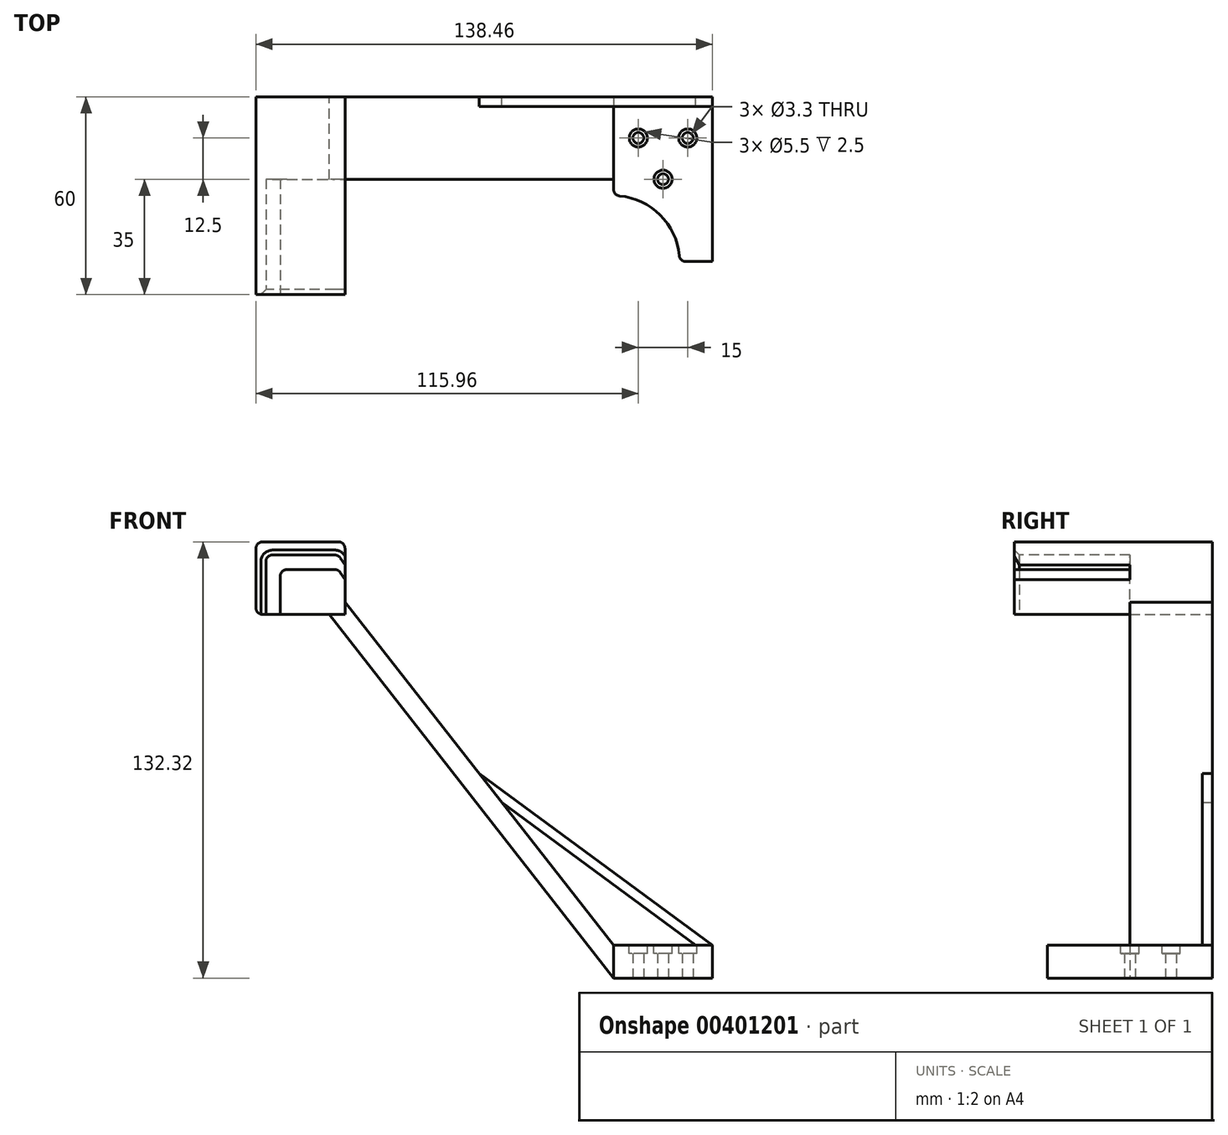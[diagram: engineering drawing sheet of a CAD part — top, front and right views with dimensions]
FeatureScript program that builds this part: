
annotation { "Feature Type Name" : "Feature", "Feature Type Description" : "" }
export const myFeature = defineFeature(function(context is Context, id is Id, definition is map)
    precondition{}
    {
        {
            var Q0;
            Q0=qCreatedBy(makeId("Top.planeOp"),FACE);
            var sketch = newSketch(context, id + "F0", { "sketchPlane" : qUnion([Q0])});
            skLineSegment(sketch, "E0.bottom", {"start": v(0, 0) * mm, "end": v(30, 0) * mm});
            skLineSegment(sketch, "E0.top", {"start": v(0, -50) * mm, "end": v(30, -50) * mm});
            skLineSegment(sketch, "E0.left", {"start": v(0, 0) * mm, "end": v(0, -50) * mm});
            skLineSegment(sketch, "E0.right", {"start": v(30, 0) * mm, "end": v(30, -50) * mm});
            skLineSegment(sketch, "E1", {"start": v(15, -50) * mm, "end": v(15, 0) * mm, "construction": true});
            skLineSegment(sketch, "E2", {"start": v(0, -25) * mm, "end": v(30, -25) * mm, "construction": true});
            skLineSegment(sketch, "E3", {"start": v(0, -12.5) * mm, "end": v(30, -12.5) * mm, "construction": true});
            skPoint(sketch, "E4", {"position": v(7.5, -12.5) * mm});
            skPoint(sketch, "E5", {"position": v(22.5, -12.5) * mm});
            skPoint(sketch, "E6", {"position": v(15, -25) * mm});
            skSolve(sketch);
        }
        {
            var Q0;
            Q0=makeQuery(id+"F0.imprint","IMPRINT",FACE,{"disambiguationData":[TD([[makeQuery(id+"F0.imprint","IMPRINT",EDGE,{"derivedFrom":sQuery(id+"F0.wireOp",EDGE,"E0.bottom")}),-1.0]])]});
            extrude(context, id + "F1", {"entities" : qUnion([Q0]), "depth" : 10 * mm, "offsetDistance" : 25 * mm});
        }
        {
            var Q0;
            Q0=qCreatedBy(makeId("Front.planeOp"),FACE);
            var sketch = newSketch(context, id + "F2", { "sketchPlane" : qUnion([Q0])});
            skLineSegment(sketch, "E7", {"start": v(0, 0) * mm, "end": v(-86.2, 110.32) * mm});
            skLineSegment(sketch, "E8", {"start": v(-86.2, 110.32) * mm, "end": v(-81.46, 114.02) * mm});
            skLineSegment(sketch, "E9", {"start": v(-81.46, 114.02) * mm, "end": v(0, 10) * mm});
            skLineSegment(sketch, "E10", {"start": v(0, 10) * mm, "end": v(0, 0) * mm});
            skLineSegment(sketch, "E11.bottom", {"start": v(-81.46, 132.32) * mm, "end": v(-108.46, 132.32) * mm});
            skLineSegment(sketch, "E11.top", {"start": v(-81.46, 110.32) * mm, "end": v(-108.46, 110.32) * mm});
            skLineSegment(sketch, "E11.left", {"start": v(-81.46, 132.32) * mm, "end": v(-81.46, 110.32) * mm});
            skLineSegment(sketch, "E11.right", {"start": v(-108.46, 132.32) * mm, "end": v(-108.46, 110.32) * mm});
            skSolve(sketch);
        }
        {
            var Q0;
            Q0=makeQuery(id+"F2.imprint","IMPRINT",FACE,{"disambiguationData":[TD([[makeQuery(id+"F2.imprint","IMPRINT",EDGE,{"derivedFrom":sQuery(id+"F2.wireOp",EDGE,"E9")}),-1.0]])]});
            extrude(context, id + "F3", {"entities" : qUnion([Q0]), "operationType" : NewBodyOperationType.ADD, "depth" : 25 * mm, "offsetDistance" : 25 * mm});
        }
        {
            var Q0;
            Q0=makeQuery(id+"F1.opExtrude","CAP_FACE",FACE,{"disambiguationData":[OSD([sQuery(id+"F0.wireOp",EDGE,"E0.bottom"),sQuery(id+"F0.wireOp",EDGE,"E0.top"),sQuery(id+"F0.wireOp",EDGE,"E0.left"),sQuery(id+"F0.wireOp",EDGE,"E0.right")])],"isStart":false});
            var sketch = newSketch(context, id + "F4", { "sketchPlane" : qUnion([Q0])});
            skCircle(sketch, "E12", {"center": v(0, -50) * mm, "radius": 20 * mm});
            skSolve(sketch);
        }
        {
            var Q0;
            Q0 = qSketchRegion(id + "F4", true);
            var Q1;
            {var subQ1=makeQuery(id+"F1.opExtrude","CAP_EDGE",EDGE,{"disambiguationData":[OSD([sQuery(id+"F0.wireOp",EDGE,"E0.left")])],"isStart":false});var subQ2=makeQuery(id+"F3.boolean.opBoolean","SPLIT",EDGE,{"derivedFrom":subQ1});Q1=makeQuery(id+"F4.imprint","IMPRINT",FACE,{"disambiguationData":[TD([[makeQuery(id+"F4.imprint","IMPRINT",EDGE,{"derivedFrom":subQ2}),1.0]])]});}
            extrude(context, id + "F5", {"entities" : qUnion([Q0, Q1]), "operationType" : NewBodyOperationType.REMOVE, "oppositeDirection" : true, "depth" : 25 * mm, "offsetDistance" : 25 * mm});
        }
        {
            var Q0;
            {var subQ4=sQuery(id+"F2.wireOp",EDGE,"E8");Q0=makeQuery(id+"F2.imprint","IMPRINT",FACE,{"disambiguationData":[TD([[makeQuery(id+"F2.imprint","IMPRINT",EDGE,{"derivedFrom":subQ4}),1.0]])]});}
            var Q1;
            {var subQ0=sQuery(id+"F2.wireOp",EDGE,"E8");Q1=makeQuery(id+"F2.imprint","IMPRINT",FACE,{"disambiguationData":[TD([[makeQuery(id+"F2.imprint","IMPRINT",EDGE,{"derivedFrom":subQ0}),-1.0]])]});}
            extrude(context, id + "F6", {"entities" : qUnion([Q0, Q1]), "depth" : 60 * mm, "offsetDistance" : 25 * mm});
        }
        {
            var Q0;
            Q0=makeQuery(id+"F6.opExtrude","CAP_FACE",FACE,{"disambiguationData":[OSD([sQuery(id+"F2.wireOp",EDGE,"E11.bottom"),sQuery(id+"F2.wireOp",EDGE,"E11.top"),sQuery(id+"F2.wireOp",EDGE,"E11.left"),sQuery(id+"F2.wireOp",EDGE,"E11.right")])],"isStart":false});
            var sketch = newSketch(context, id + "F7", { "sketchPlane" : qUnion([Q0])});
            skLineSegment(sketch, "E13", {"start": v(-105.46, 110.32) * mm, "end": v(-105.46, 128.32) * mm});
            skLineSegment(sketch, "E14", {"start": v(-105.46, 128.32) * mm, "end": v(-83.46, 128.32) * mm});
            skLineSegment(sketch, "E15", {"start": v(-83.46, 128.32) * mm, "end": v(-81.46, 125.3) * mm});
            skLineSegment(sketch, "E16", {"start": v(-101.06, 110.32) * mm, "end": v(-101.06, 123.92) * mm});
            skLineSegment(sketch, "E17", {"start": v(-101.06, 123.92) * mm, "end": v(-83.46, 123.92) * mm});
            skLineSegment(sketch, "E18", {"start": v(-83.46, 123.92) * mm, "end": v(-81.46, 120.9) * mm});
            skSolve(sketch);
        }
        {
            var Q0;
            {var subQ4=sQuery(id+"F7.wireOp",EDGE,"E13");Q0=makeQuery(id+"F7.imprint","IMPRINT",FACE,{"disambiguationData":[TD([[makeQuery(id+"F7.imprint","IMPRINT",EDGE,{"derivedFrom":subQ4}),-1.0]])]});}
            extrude(context, id + "F8", {"entities" : qUnion([Q0]), "operationType" : NewBodyOperationType.REMOVE, "oppositeDirection" : true, "depth" : 35 * mm, "offsetDistance" : 25 * mm});
        }
        {
            var Q0;
            Q0=makeQuery(id+"F8.boolean.opBoolean","COPY",EDGE,{"derivedFrom":makeQuery(id+"F8.opExtrude","SWEPT_EDGE",EDGE,{"disambiguationData":[OSD([sQuery(id+"F2.wireOp",EDGE,"E11.top"),sQuery(id+"F7.wireOp",EDGE,"E16")])]})});
            var Q1;
            Q1=makeQuery(id+"F8.boolean.opBoolean","COPY",EDGE,{"derivedFrom":makeQuery(id+"F8.opExtrude","SWEPT_EDGE",EDGE,{"disambiguationData":[OSD([sQuery(id+"F7.wireOp",EDGE,"E16"),sQuery(id+"F7.wireOp",EDGE,"E17")])]})});
            var Q2;
            Q2=makeQuery(id+"F8.boolean.opBoolean","COPY",EDGE,{"derivedFrom":makeQuery(id+"F8.opExtrude","SWEPT_EDGE",EDGE,{"disambiguationData":[OSD([sQuery(id+"F7.wireOp",EDGE,"E13"),sQuery(id+"F7.wireOp",EDGE,"E14")])]})});
            var Q3;
            Q3=makeQuery(id+"F8.boolean.opBoolean","COPY",EDGE,{"derivedFrom":makeQuery(id+"F8.opExtrude","SWEPT_EDGE",EDGE,{"disambiguationData":[OSD([sQuery(id+"F7.wireOp",EDGE,"E14"),sQuery(id+"F7.wireOp",EDGE,"E15")])]})});
            var Q4;
            Q4=makeQuery(id+"F8.boolean.opBoolean","COPY",EDGE,{"derivedFrom":makeQuery(id+"F8.opExtrude","SWEPT_EDGE",EDGE,{"disambiguationData":[OSD([sQuery(id+"F7.wireOp",EDGE,"E17"),sQuery(id+"F7.wireOp",EDGE,"E18")])]})});
            var Q5;
            Q5=makeQuery(id+"F6.opExtrude","SWEPT_EDGE",EDGE,{"disambiguationData":[OSD([sQuery(id+"F2.wireOp",EDGE,"E11.bottom"),sQuery(id+"F2.wireOp",EDGE,"E11.left")])]});
            var Q6;
            Q6=makeQuery(id+"F6.opExtrude","SWEPT_EDGE",EDGE,{"disambiguationData":[OSD([sQuery(id+"F2.wireOp",EDGE,"E11.bottom"),sQuery(id+"F2.wireOp",EDGE,"E11.right")])]});
            var Q7;
            Q7=makeQuery(id+"F6.opExtrude","SWEPT_EDGE",EDGE,{"disambiguationData":[OSD([sQuery(id+"F2.wireOp",EDGE,"E11.top"),sQuery(id+"F2.wireOp",EDGE,"E11.right")])]});
            var Q8;
            Q8=makeQuery(id+"F8.boolean.opBoolean","COPY",EDGE,{"derivedFrom":makeQuery(id+"F8.opExtrude","SWEPT_EDGE",EDGE,{"disambiguationData":[OSD([sQuery(id+"F2.wireOp",EDGE,"E11.left"),sQuery(id+"F7.wireOp",EDGE,"E18")])]})});
            var Q9;
            Q9=makeQuery(id+"F8.boolean.opBoolean","COPY",EDGE,{"derivedFrom":makeQuery(id+"F8.opExtrude","SWEPT_EDGE",EDGE,{"disambiguationData":[OSD([sQuery(id+"F2.wireOp",EDGE,"E11.top"),sQuery(id+"F7.wireOp",EDGE,"E13")])]})});
            var Q10;
            Q10=makeQuery(id+"F3.opExtrude","CAP_EDGE",EDGE,{"disambiguationData":[OSD([sQuery(id+"F2.wireOp",EDGE,"E10")])],"isStart":false});
            var Q11;
            Q11=makeQuery(id+"F5.boolean.opBoolean","INTERSECT",EDGE,{"derivedFrom":[makeQuery(id+"F1.opExtrude","SWEPT_FACE",FACE,{"disambiguationData":[OSD([sQuery(id+"F0.wireOp",EDGE,"E0.left")])]}),makeQuery(id+"F5.opExtrude","SWEPT_FACE",FACE,{"disambiguationData":[OSD([sQuery(id+"F4.wireOp",EDGE,"E12")])]})]});
            var Q12;
            Q12=makeQuery(id+"F5.boolean.opBoolean","INTERSECT",EDGE,{"derivedFrom":[makeQuery(id+"F1.opExtrude","SWEPT_FACE",FACE,{"disambiguationData":[OSD([sQuery(id+"F0.wireOp",EDGE,"E0.top")])]}),makeQuery(id+"F5.opExtrude","SWEPT_FACE",FACE,{"disambiguationData":[OSD([sQuery(id+"F4.wireOp",EDGE,"E12")])]})]});
            fillet(context, id + "F9", {"entities" : qUnion([Q0, Q1, Q2, Q3, Q4, Q5, Q6, Q7, Q8, Q9, Q10, Q11, Q12]), "radius" : 2 * mm, "tangentPropagation" : true, "allowEdgeOverflow" : false});
        }
        {
            var Q0;
            Q0=makeQuery(id+"F8.boolean.opBoolean","COPY",EDGE,{"derivedFrom":makeQuery(id+"F8.opExtrude","CAP_EDGE",EDGE,{"disambiguationData":[OSD([sQuery(id+"F7.wireOp",EDGE,"E13")])],"isStart":true})});
            var Q1;
            Q1=makeQuery(id+"F8.boolean.opBoolean","COPY",EDGE,{"derivedFrom":makeQuery(id+"F8.opExtrude","CAP_EDGE",EDGE,{"disambiguationData":[OSD([sQuery(id+"F7.wireOp",EDGE,"E17")])],"isStart":true})});
            chamfer(context, id + "F10", {"entities" : qUnion([Q0, Q1]), "width" : 1.5 * mm, "tangentPropagation" : true});
        }
        {
            var Q0;
            Q0=makeQuery(id+"F3.boolean.opBoolean","MERGE",FACE,{"derivedFrom":[makeQuery(id+"F1.opExtrude","SWEPT_FACE",FACE,{"disambiguationData":[OSD([sQuery(id+"F0.wireOp",EDGE,"E0.bottom")])]}),makeQuery(id+"F3.opExtrude","CAP_FACE",FACE,{"disambiguationData":[OSD([sQuery(id+"F2.wireOp",EDGE,"E7"),sQuery(id+"F2.wireOp",EDGE,"E9"),sQuery(id+"F2.wireOp",EDGE,"E10"),sQuery(id+"F2.wireOp",EDGE,"E11.top"),sQuery(id+"F2.wireOp",EDGE,"E11.left")])],"isStart":true})]});
            var sketch = newSketch(context, id + "F11", { "sketchPlane" : qUnion([Q0])});
            skLineSegment(sketch, "E19", {"start": v(-30, 10) * mm, "end": v(40.73, 62) * mm});
            skLineSegment(sketch, "E20", {"start": v(-24.94, 10) * mm, "end": v(33.86, 53.23) * mm});
            skSolve(sketch);
        }
        {
            var Q0;
            {var subQ0=sQuery(id+"F11.wireOp",EDGE,"E19");Q0=makeQuery(id+"F11.imprint","IMPRINT",FACE,{"disambiguationData":[TD([[makeQuery(id+"F11.imprint","IMPRINT",EDGE,{"derivedFrom":subQ0}),-1.0]])]});}
            extrude(context, id + "F12", {"entities" : qUnion([Q0]), "operationType" : NewBodyOperationType.ADD, "oppositeDirection" : true, "depth" : 3 * mm, "offsetDistance" : 25 * mm});
        }
        {
            var Q0;
            Q0=sQuery(id+"F0.wireOp",VERTEX,"E4");
            var Q1;
            Q1=sQuery(id+"F0.wireOp",VERTEX,"E5");
            var Q2;
            Q2=sQuery(id+"F0.wireOp",VERTEX,"E6");
            var Q3;
            Q3=makeQuery(id+"F1.opExtrude","SWEPT_BODY",BODY,{"disambiguationData":[OSD([sQuery(id+"F0.wireOp",EDGE,"E0.bottom"),sQuery(id+"F0.wireOp",EDGE,"E0.top"),sQuery(id+"F0.wireOp",EDGE,"E0.left"),sQuery(id+"F0.wireOp",EDGE,"E0.right")])]});
            hole(context, id + "F13", {"style" : HoleStyle.SIMPLE, "endStyle" : HoleEndStyle.THROUGH, "oppositeDirection" : true, "standardTappedOrClearance" : lookupTablePath({ "standard" : "ISO", "fit" : "Normal", "size" : "M3", "type" : "Clearance" }), "standardBlindInLast" : lookupTablePath({ "fit" : "Standard", "standard" : "ISO", "size" : "M3", "type" : "Clearance" }), "holeDiameter" : 3.3 * mm, "majorDiameter" : 5 * mm, "isTappedThrough" : true, "tappedDepth" : 12 * mm, "tapClearance" : 3, "locations" : qUnion([Q0, Q1, Q2]), "scope" : qUnion([Q3])});
        }
        {
            var Q0;
            Q0=makeQuery(id+"F1.opExtrude","CAP_FACE",FACE,{"disambiguationData":[OSD([sQuery(id+"F0.wireOp",EDGE,"E0.bottom"),sQuery(id+"F0.wireOp",EDGE,"E0.top"),sQuery(id+"F0.wireOp",EDGE,"E0.left"),sQuery(id+"F0.wireOp",EDGE,"E0.right")])],"isStart":false});
            var sketch = newSketch(context, id + "F14", { "sketchPlane" : qUnion([Q0])});
            skCircle(sketch, "E21", {"center": v(22.5, -12.5) * mm, "radius": 2.75 * mm});
            skCircle(sketch, "E22", {"center": v(7.5, -12.5) * mm, "radius": 2.75 * mm});
            skCircle(sketch, "E23", {"center": v(15, -25) * mm, "radius": 2.75 * mm});
            skSolve(sketch);
        }
        {
            var Q0;
            Q0 = qSketchRegion(id + "F14", true);
            extrude(context, id + "F15", {"entities" : qUnion([Q0]), "operationType" : NewBodyOperationType.REMOVE, "oppositeDirection" : true, "depth" : 2.5 * mm, "offsetDistance" : 25 * mm});
        }
    });
